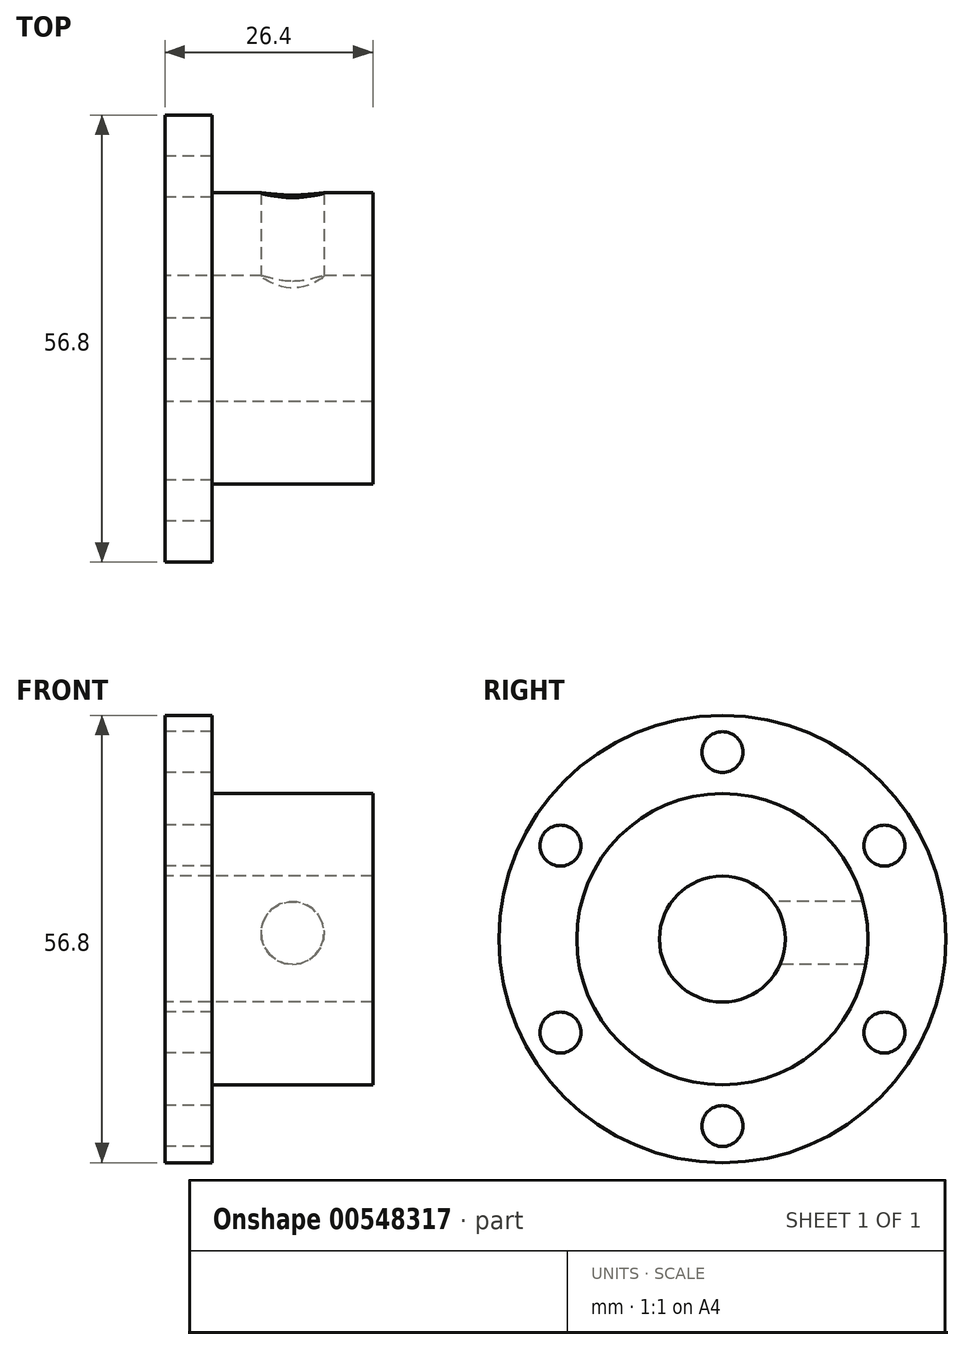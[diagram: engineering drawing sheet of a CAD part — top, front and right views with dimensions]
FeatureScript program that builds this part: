
annotation { "Feature Type Name" : "Feature", "Feature Type Description" : "" }
export const myFeature = defineFeature(function(context is Context, id is Id, definition is map)
    precondition{}
    {
        {
            var Q0;
            Q0=qCreatedBy(makeId("Front.planeOp"),FACE);
            var sketch = newSketch(context, id + "F0", { "sketchPlane" : qUnion([Q0])});
            skLineSegment(sketch, "E0", {"start": v(8.2, -2.84) * mm, "end": v(-18.2, -2.84) * mm});
            skLineSegment(sketch, "E1", {"start": v(-18.2, -2.84) * mm, "end": v(-18.2, 17.56) * mm});
            skLineSegment(sketch, "E2", {"start": v(-18.2, 17.56) * mm, "end": v(-12.2, 17.56) * mm});
            skLineSegment(sketch, "E3", {"start": v(-12.2, 17.56) * mm, "end": v(-12.2, 7.66) * mm});
            skLineSegment(sketch, "E4", {"start": v(-12.2, 7.66) * mm, "end": v(8.2, 7.66) * mm});
            skLineSegment(sketch, "E5", {"start": v(8.2, 7.66) * mm, "end": v(8.2, -2.84) * mm});
            skLineSegment(sketch, "E6", {"start": v(-18.2, -10.84) * mm, "end": v(24.04, -10.84) * mm});
            skSolve(sketch);
        }
        {
            var Q0;
            Q0=makeQuery(id+"F0.imprint","IMPRINT",FACE,{"disambiguationData":[TD([[makeQuery(id+"F0.imprint","IMPRINT",EDGE,{"derivedFrom":sQuery(id+"F0.wireOp",EDGE,"E0")}),-1.0]])]});
            var Q1;
            Q1=sQuery(id+"F0.wireOp",EDGE,"E6");
            revolve(context, id + "F1", {"entities" : qUnion([Q0]), "axis" : qUnion([Q1]), "revolveType" : RevolveType.FULL});
        }
        {
            var Q0;
            Q0=makeQuery(id+"F1.opRevolve","SWEPT_FACE",FACE,{"disambiguationData":[OSD([sQuery(id+"F0.wireOp",EDGE,"E1")])]});
            var sketch = newSketch(context, id + "F2", { "sketchPlane" : qUnion([Q0])});
            skCircle(sketch, "E7", {"center": v(0, -10.84) * mm, "radius": 23.75 * mm, "construction": true});
            skCircle(sketch, "E8", {"center": v(0, 12.9) * mm, "radius": 2.6 * mm});
            skCircle(sketch, "E9.1.0", {"center": v(-20.57, 1.03) * mm, "radius": 2.6 * mm});
            skCircle(sketch, "E9.2.0", {"center": v(-20.57, -22.72) * mm, "radius": 2.6 * mm});
            skCircle(sketch, "E9.3.0", {"center": v(0, -34.6) * mm, "radius": 2.6 * mm});
            skCircle(sketch, "E9.4.0", {"center": v(20.57, -22.72) * mm, "radius": 2.6 * mm});
            skCircle(sketch, "E9.5.0", {"center": v(20.57, 1.03) * mm, "radius": 2.6 * mm});
            skSolve(sketch);
        }
        {
            var Q0;
            Q0=makeQuery(id+"F2.imprint","IMPRINT",FACE,{"disambiguationData":[TD([[makeQuery(id+"F2.imprint","IMPRINT",EDGE,{"derivedFrom":sQuery(id+"F2.wireOp",EDGE,"E8")}),1.0]])]});
            var Q1;
            Q1=makeQuery(id+"F2.imprint","IMPRINT",FACE,{"disambiguationData":[TD([[makeQuery(id+"F2.imprint","IMPRINT",EDGE,{"derivedFrom":sQuery(id+"F2.wireOp",EDGE,"E9.1.0")}),1.0]])]});
            var Q2;
            Q2=makeQuery(id+"F2.imprint","IMPRINT",FACE,{"disambiguationData":[TD([[makeQuery(id+"F2.imprint","IMPRINT",EDGE,{"derivedFrom":sQuery(id+"F2.wireOp",EDGE,"E9.2.0")}),1.0]])]});
            var Q3;
            Q3=makeQuery(id+"F2.imprint","IMPRINT",FACE,{"disambiguationData":[TD([[makeQuery(id+"F2.imprint","IMPRINT",EDGE,{"derivedFrom":sQuery(id+"F2.wireOp",EDGE,"E9.3.0")}),1.0]])]});
            var Q4;
            Q4=makeQuery(id+"F2.imprint","IMPRINT",FACE,{"disambiguationData":[TD([[makeQuery(id+"F2.imprint","IMPRINT",EDGE,{"derivedFrom":sQuery(id+"F2.wireOp",EDGE,"E9.4.0")}),1.0]])]});
            var Q5;
            Q5=makeQuery(id+"F2.imprint","IMPRINT",FACE,{"disambiguationData":[TD([[makeQuery(id+"F2.imprint","IMPRINT",EDGE,{"derivedFrom":sQuery(id+"F2.wireOp",EDGE,"E9.5.0")}),1.0]])]});
            var Q6;
            Q6=sQuery(id+"F2.wireOp",EDGE,"E8");
            extrude(context, id + "F3", {"entities" : qUnion([Q0, Q1, Q2, Q3, Q4, Q5]), "operationType" : NewBodyOperationType.REMOVE, "surfaceEntities" : qUnion([Q6]), "oppositeDirection" : true, "depth" : 25 * mm, "offsetDistance" : 25 * mm});
        }
        {
            var Q0;
            Q0=qCreatedBy(makeId("Front.planeOp"),FACE);
            var sketch = newSketch(context, id + "F4", { "sketchPlane" : qUnion([Q0])});
            skCircle(sketch, "E10", {"center": v(-2, -10.07) * mm, "radius": 4 * mm});
            skSolve(sketch);
        }
        {
            var Q0;
            Q0=qSketchRegion(id+"F4",true);
            extrude(context, id + "F5", {"entities" : qUnion([Q0]), "operationType" : NewBodyOperationType.REMOVE, "oppositeDirection" : true, "depth" : 25 * mm, "offsetDistance" : 25 * mm});
        }
    });
